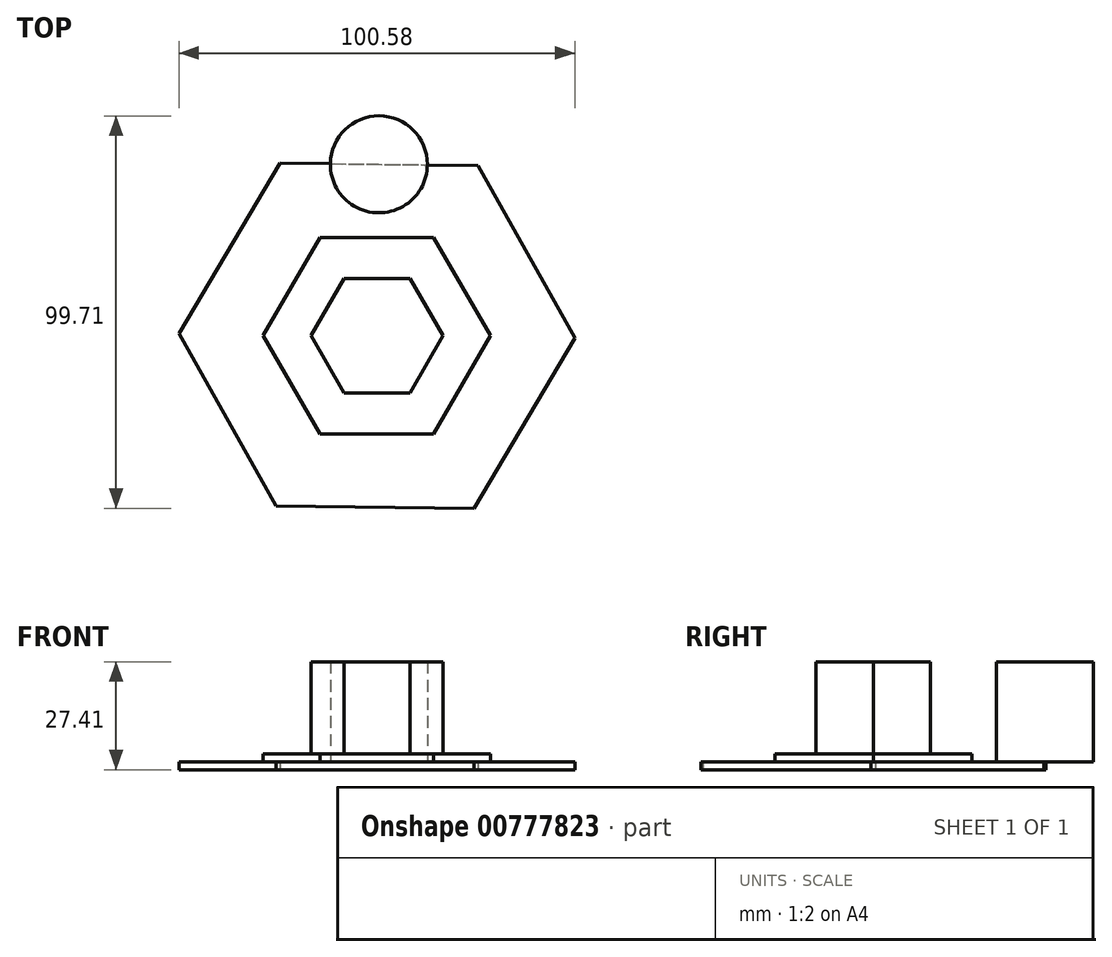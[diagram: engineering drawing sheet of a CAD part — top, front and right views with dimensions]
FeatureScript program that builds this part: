
annotation { "Feature Type Name" : "Feature", "Feature Type Description" : "" }
export const myFeature = defineFeature(function(context is Context, id is Id, definition is map)
    precondition{}
    {
        {
            var Q0;
            Q0=qCreatedBy(makeId("Top.planeOp"),FACE);
            var sketch = newSketch(context, id + "F0", { "sketchPlane" : qUnion([Q0])});
            skCircle(sketch, "E0.cCircle", {"center": v(0, 0) * mm, "radius": 43.56 * mm, "construction": true});
            skLineSegment(sketch, "E0.0", {"start": v(-50.3, 0.58) * mm, "end": v(-24.64, 43.84) * mm});
            skLineSegment(sketch, "E0.1", {"start": v(-24.64, 43.84) * mm, "end": v(25.65, 43.26) * mm});
            skLineSegment(sketch, "E0.2", {"start": v(25.65, 43.26) * mm, "end": v(50.3, -0.58) * mm});
            skLineSegment(sketch, "E0.3", {"start": v(50.3, -0.58) * mm, "end": v(24.64, -43.84) * mm});
            skLineSegment(sketch, "E0.4", {"start": v(24.64, -43.84) * mm, "end": v(-25.65, -43.26) * mm});
            skLineSegment(sketch, "E0.5", {"start": v(-25.65, -43.26) * mm, "end": v(-50.3, 0.58) * mm});
            skPoint(sketch, "E0.0.midPoint", {"position": v(-37.47, 22.21) * mm});
            skSolve(sketch);
        }
        {
            var Q0;
            Q0=makeQuery(id+"F0.imprint","IMPRINT",FACE,{"disambiguationData":[TD([[makeQuery(id+"F0.imprint","IMPRINT",EDGE,{"derivedFrom":sQuery(id+"F0.wireOp",EDGE,"E0.0")}),-1.0]])]});
            extrude(context, id + "F1", {"entities" : qUnion([Q0]), "depth" : 2 * mm, "offsetDistance" : 25.4 * mm});
        }
        {
            var Q0;
            Q0=makeQuery(id+"F1.opExtrude","CAP_FACE",FACE,{"disambiguationData":[OSD([sQuery(id+"F0.wireOp",EDGE,"E0.0"),sQuery(id+"F0.wireOp",EDGE,"E0.1"),sQuery(id+"F0.wireOp",EDGE,"E0.2"),sQuery(id+"F0.wireOp",EDGE,"E0.3"),sQuery(id+"F0.wireOp",EDGE,"E0.4"),sQuery(id+"F0.wireOp",EDGE,"E0.5")])],"isStart":false});
            var sketch = newSketch(context, id + "F2", { "sketchPlane" : qUnion([Q0])});
            skCircle(sketch, "E1.cCircle", {"center": v(0, 0) * mm, "radius": 25 * mm, "construction": true});
            skLineSegment(sketch, "E1.0", {"start": v(-14.44, 25) * mm, "end": v(14.44, 25) * mm});
            skLineSegment(sketch, "E1.1", {"start": v(14.44, 25) * mm, "end": v(28.87, 0) * mm});
            skLineSegment(sketch, "E1.2", {"start": v(28.87, 0) * mm, "end": v(14.44, -25) * mm});
            skLineSegment(sketch, "E1.3", {"start": v(14.44, -25) * mm, "end": v(-14.44, -25) * mm});
            skLineSegment(sketch, "E1.4", {"start": v(-14.44, -25) * mm, "end": v(-28.87, 0) * mm});
            skLineSegment(sketch, "E1.5", {"start": v(-28.87, 0) * mm, "end": v(-14.44, 25) * mm});
            skPoint(sketch, "E1.0.midPoint", {"position": v(0, 25) * mm});
            skSolve(sketch);
        }
        {
            var Q0;
            Q0 = qSketchRegion(id + "F2", true);
            extrude(context, id + "F3", {"entities" : qUnion([Q0]), "operationType" : NewBodyOperationType.ADD, "depth" : 2 * mm, "offsetDistance" : 25.4 * mm});
        }
        {
            var Q0;
            Q0=makeQuery(id+"F1.opExtrude","CAP_FACE",FACE,{"disambiguationData":[OSD([sQuery(id+"F0.wireOp",EDGE,"E0.0"),sQuery(id+"F0.wireOp",EDGE,"E0.1"),sQuery(id+"F0.wireOp",EDGE,"E0.2"),sQuery(id+"F0.wireOp",EDGE,"E0.3"),sQuery(id+"F0.wireOp",EDGE,"E0.4"),sQuery(id+"F0.wireOp",EDGE,"E0.5")])],"isStart":false});
            var sketch = newSketch(context, id + "F4", { "sketchPlane" : qUnion([Q0])});
            skCircle(sketch, "E2.cCircle", {"center": v(0, 0) * mm, "radius": 14.54 * mm, "construction": true});
            skLineSegment(sketch, "E2.0", {"start": v(-8.4, 14.54) * mm, "end": v(8.4, 14.54) * mm});
            skLineSegment(sketch, "E2.1", {"start": v(8.4, 14.54) * mm, "end": v(16.79, 0) * mm});
            skLineSegment(sketch, "E2.2", {"start": v(16.79, 0) * mm, "end": v(8.4, -14.54) * mm});
            skLineSegment(sketch, "E2.3", {"start": v(8.4, -14.54) * mm, "end": v(-8.4, -14.54) * mm});
            skLineSegment(sketch, "E2.4", {"start": v(-8.4, -14.54) * mm, "end": v(-16.79, 0) * mm});
            skLineSegment(sketch, "E2.5", {"start": v(-16.79, 0) * mm, "end": v(-8.4, 14.54) * mm});
            skPoint(sketch, "E2.0.midPoint", {"position": v(0, 14.54) * mm});
            skCircle(sketch, "E3", {"center": v(0.5, 43.55) * mm, "radius": 12.32 * mm});
            skSolve(sketch);
        }
        {
            var Q0;
            Q0=makeQuery(id+"F4.imprint","IMPRINT",FACE,{"disambiguationData":[TD([[makeQuery(id+"F4.imprint","IMPRINT",EDGE,{"derivedFrom":sQuery(id+"F4.wireOp",EDGE,"E2.0")}),-1.0]])]});
            var Q1;
            {var subQ0=sQuery(id+"F4.wireOp",EDGE,"E3");var subQ1=makeQuery(id+"F1.opExtrude","CAP_EDGE",EDGE,{"disambiguationData":[OSD([sQuery(id+"F0.wireOp",EDGE,"E0.1")])],"isStart":false});var subQ2=makeQuery(id+"F4.imprint","INTERSECT",VERTEX,{"disambiguationData":[OD(0.0)],"derivedFrom":[subQ1,subQ0]});Q1=makeQuery(id+"F4.imprint","IMPRINT",FACE,{"disambiguationData":[TD([[makeQuery(id+"F4.imprint","IMPRINT",EDGE,{"disambiguationData":[TD([[subQ2,-1.0]])],"derivedFrom":subQ0}),1.0]])]});}
            var Q2;
            {var subQ0=sQuery(id+"F4.wireOp",EDGE,"E3");var subQ1=makeQuery(id+"F1.opExtrude","CAP_EDGE",EDGE,{"disambiguationData":[OSD([sQuery(id+"F0.wireOp",EDGE,"E0.1")])],"isStart":false});var subQ2=makeQuery(id+"F4.imprint","INTERSECT",VERTEX,{"disambiguationData":[OD(0.0)],"derivedFrom":[subQ1,subQ0]});Q2=makeQuery(id+"F4.imprint","IMPRINT",FACE,{"disambiguationData":[TD([[makeQuery(id+"F4.imprint","IMPRINT",EDGE,{"disambiguationData":[TD([[subQ2,1.0]])],"derivedFrom":subQ0}),1.0]])]});}
            extrude(context, id + "F5", {"entities" : qUnion([Q0, Q1, Q2]), "operationType" : NewBodyOperationType.ADD, "depth" : 25.4 * mm, "offsetDistance" : 25.4 * mm});
        }
    });
